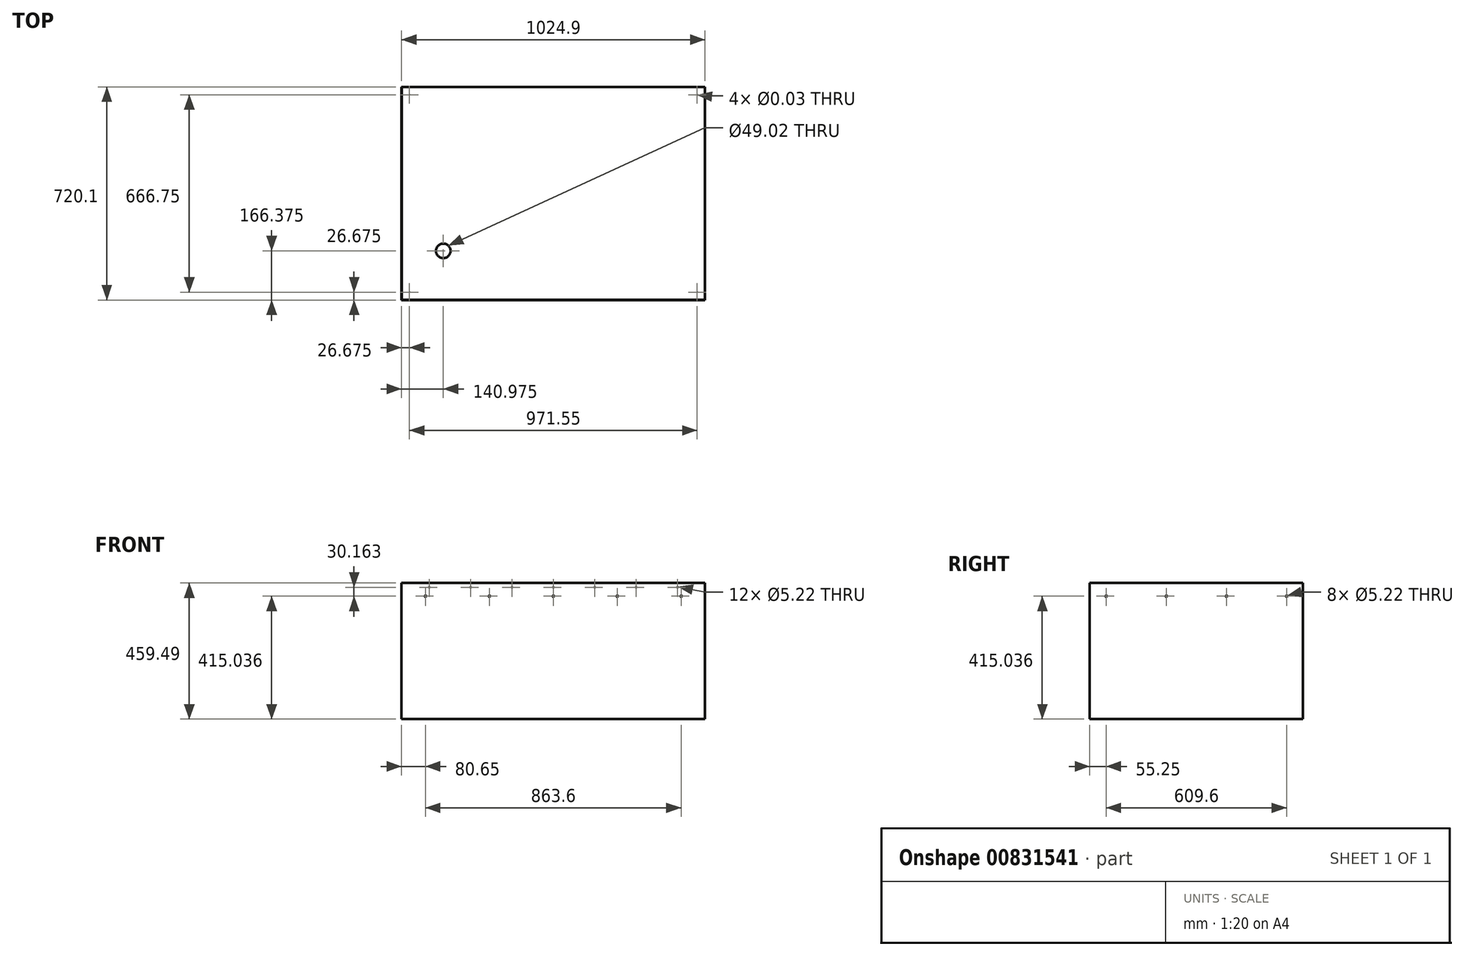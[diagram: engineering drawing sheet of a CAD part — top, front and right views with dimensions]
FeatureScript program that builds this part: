
annotation { "Feature Type Name" : "Feature", "Feature Type Description" : "" }
export const myFeature = defineFeature(function(context is Context, id is Id, definition is map)
    precondition{}
    {
        {
            var Q0;
            Q0=qCreatedBy(makeId("Top.planeOp"),FACE);
            var sketch = newSketch(context, id + "F0", { "sketchPlane" : qUnion([Q0])});
            skLineSegment(sketch, "E0.bottom", {"start": v(-512.45, 360.05) * mm, "end": v(512.45, 360.05) * mm});
            skLineSegment(sketch, "E0.top", {"start": v(-512.45, -360.05) * mm, "end": v(512.45, -360.05) * mm});
            skLineSegment(sketch, "E0.left", {"start": v(-512.44, 360.04) * mm, "end": v(-512.45, -360.05) * mm});
            skLineSegment(sketch, "E0.right", {"start": v(512.45, 360.05) * mm, "end": v(512.44, -360.05) * mm});
            skLineSegment(sketch, "E1", {"start": v(0, 360.05) * mm, "end": v(0, 0) * mm});
            skLineSegment(sketch, "E2", {"start": v(0, 0) * mm, "end": v(0, -360.05) * mm});
            skSolve(sketch);
        }
        {
            var Q0;
            Q0=makeQuery(id+"F0.imprint","IMPRINT",FACE,{"disambiguationData":[TD([[makeQuery(id+"F0.imprint","IMPRINT",EDGE,{"derivedFrom":sQuery(id+"F0.wireOp",EDGE,"E0.bottom")}),-1.0]])]});
            extrude(context, id + "F1", {"entities" : qUnion([Q0]), "depth" : 459.5 * mm, "offsetDistance" : 25.4 * mm});
        }
        {
            var Q0;
            Q0=makeQuery(id+"F1.opExtrude","CAP_FACE",FACE,{"disambiguationData":[OSD([sQuery(id+"F0.wireOp",EDGE,"E0.bottom"),sQuery(id+"F0.wireOp",EDGE,"E0.top"),sQuery(id+"F0.wireOp",EDGE,"E0.left"),sQuery(id+"F0.wireOp",EDGE,"E0.right"),sQuery(id+"F0.wireOp",EDGE,"5e8189b1-4f6e-42a7-91f4-dac5e5891543.filletArc"),sQuery(id+"F0.wireOp",EDGE,"1cc928d6-0298-44d3-bfd6-6e0c63f41985.filletArc"),sQuery(id+"F0.wireOp",EDGE,"5963119c-fd0b-4c36-9543-9db4226832d0.filletArc"),sQuery(id+"F0.wireOp",EDGE,"1aff30c5-95b7-47c3-b3d6-6abb8407ea33.filletArc")])],"isStart":false});
            shell(context, id + "F2", {"entities" : qUnion([Q0]), "thickness" : 0.76 * mm});
        }
        {
            var Q0;
            Q0=makeQuery(id+"F1.opExtrude","SWEPT_FACE",FACE,{"disambiguationData":[OSD([sQuery(id+"F0.wireOp",EDGE,"E0.top")])]});
            var sketch = newSketch(context, id + "F3", { "sketchPlane" : qUnion([Q0])});
            skPoint(sketch, "E3", {"position": v(-431.8, 415.04) * mm});
            skPoint(sketch, "E4", {"position": v(-215.9, 415.04) * mm});
            skPoint(sketch, "E5", {"position": v(0, 415.04) * mm});
            skPoint(sketch, "E6", {"position": v(215.9, 415.04) * mm});
            skPoint(sketch, "E7", {"position": v(431.8, 415.04) * mm});
            skLineSegment(sketch, "E8", {"start": v(-431.8, 415.04) * mm, "end": v(-215.9, 415.04) * mm});
            skLineSegment(sketch, "E9", {"start": v(0, 415.04) * mm, "end": v(-215.9, 415.04) * mm});
            skLineSegment(sketch, "E10", {"start": v(0, 415.04) * mm, "end": v(215.9, 415.04) * mm});
            skLineSegment(sketch, "E11", {"start": v(431.8, 415.04) * mm, "end": v(215.9, 415.04) * mm});
            skLineSegment(sketch, "E12", {"start": v(0, 459.49) * mm, "end": v(0, 415.04) * mm});
            skSolve(sketch);
        }
        {
            var Q0;
            Q0=makeQuery(id+"F1.opExtrude","SWEPT_FACE",FACE,{"disambiguationData":[OSD([sQuery(id+"F0.wireOp",EDGE,"E0.right")])]});
            var sketch = newSketch(context, id + "F4", { "sketchPlane" : qUnion([Q0])});
            skPoint(sketch, "E13", {"position": v(-304.8, 415.04) * mm});
            skPoint(sketch, "E14", {"position": v(-101.6, 415.04) * mm});
            skPoint(sketch, "E15", {"position": v(101.6, 415.04) * mm});
            skPoint(sketch, "E16", {"position": v(304.8, 415.04) * mm});
            skLineSegment(sketch, "E17", {"start": v(-304.8, 415.04) * mm, "end": v(-101.6, 415.04) * mm});
            skLineSegment(sketch, "E18", {"start": v(101.6, 415.04) * mm, "end": v(304.8, 415.04) * mm});
            skLineSegment(sketch, "E19", {"start": v(-101.6, 415.04) * mm, "end": v(101.6, 415.04) * mm});
            skLineSegment(sketch, "E20", {"start": v(0, 459.49) * mm, "end": v(0, 415.04) * mm});
            skSolve(sketch);
        }
        {
            var Q0;
            Q0=sQuery(id+"F3.wireOp",VERTEX,"E3");
            var Q1;
            Q1=sQuery(id+"F3.wireOp",VERTEX,"E4");
            var Q2;
            Q2=sQuery(id+"F3.wireOp",VERTEX,"E5");
            var Q3;
            Q3=sQuery(id+"F3.wireOp",VERTEX,"E6");
            var Q4;
            Q4=sQuery(id+"F3.wireOp",VERTEX,"E7");
            var Q5;
            Q5=makeQuery(id+"F1.opExtrude","SWEPT_BODY",BODY,{"disambiguationData":[OSD([sQuery(id+"F0.wireOp",EDGE,"E0.bottom"),sQuery(id+"F0.wireOp",EDGE,"E0.top"),sQuery(id+"F0.wireOp",EDGE,"E0.left"),sQuery(id+"F0.wireOp",EDGE,"E0.right"),sQuery(id+"F0.wireOp",EDGE,"5e8189b1-4f6e-42a7-91f4-dac5e5891543.filletArc"),sQuery(id+"F0.wireOp",EDGE,"1cc928d6-0298-44d3-bfd6-6e0c63f41985.filletArc"),sQuery(id+"F0.wireOp",EDGE,"5963119c-fd0b-4c36-9543-9db4226832d0.filletArc"),sQuery(id+"F0.wireOp",EDGE,"1aff30c5-95b7-47c3-b3d6-6abb8407ea33.filletArc")])]});
            hole(context, id + "F5", {"style" : HoleStyle.SIMPLE, "endStyle" : HoleEndStyle.BLIND, "standardTappedOrClearance" : lookupTablePath({ "standard" : "ANSI", "size" : "#5 (0.2)", "type" : "Drilled" }), "standardBlindInLast" : lookupTablePath({ "standard" : "ANSI", "size" : "#5 (0.2)", "type" : "Drilled" }), "holeDiameter" : 5.22 * mm, "majorDiameter" : 6.35 * mm, "holeDepth" : 0.76 * mm, "isTappedThrough" : true, "tappedDepth" : 12.7 * mm, "tapClearance" : 3, "locations" : qUnion([Q0, Q1, Q2, Q3, Q4]), "scope" : qUnion([Q5])});
        }
        {
            var Q0;
            Q0=sQuery(id+"F4.wireOp",VERTEX,"E13");
            var Q1;
            Q1=sQuery(id+"F4.wireOp",VERTEX,"E14");
            var Q2;
            Q2=sQuery(id+"F4.wireOp",VERTEX,"E15");
            var Q3;
            Q3=sQuery(id+"F4.wireOp",VERTEX,"E16");
            var Q4;
            Q4=makeQuery(id+"F1.opExtrude","SWEPT_BODY",BODY,{"disambiguationData":[OSD([sQuery(id+"F0.wireOp",EDGE,"E0.bottom"),sQuery(id+"F0.wireOp",EDGE,"E0.top"),sQuery(id+"F0.wireOp",EDGE,"E0.left"),sQuery(id+"F0.wireOp",EDGE,"E0.right"),sQuery(id+"F0.wireOp",EDGE,"5e8189b1-4f6e-42a7-91f4-dac5e5891543.filletArc"),sQuery(id+"F0.wireOp",EDGE,"1cc928d6-0298-44d3-bfd6-6e0c63f41985.filletArc"),sQuery(id+"F0.wireOp",EDGE,"5963119c-fd0b-4c36-9543-9db4226832d0.filletArc"),sQuery(id+"F0.wireOp",EDGE,"1aff30c5-95b7-47c3-b3d6-6abb8407ea33.filletArc")])]});
            hole(context, id + "F6", {"style" : HoleStyle.SIMPLE, "endStyle" : HoleEndStyle.THROUGH, "standardTappedOrClearance" : lookupTablePath({ "standard" : "ANSI", "size" : "#5 (0.2)", "type" : "Drilled" }), "standardBlindInLast" : lookupTablePath({ "standard" : "ANSI", "size" : "#5 (0.2)", "type" : "Drilled" }), "holeDiameter" : 5.22 * mm, "majorDiameter" : 6.35 * mm, "isTappedThrough" : true, "tappedDepth" : 12.7 * mm, "tapClearance" : 3, "locations" : qUnion([Q0, Q1, Q2, Q3]), "scope" : qUnion([Q4])});
        }
        {
            var Q0;
            Q0=makeQuery(id+"F2.opShell","OFFSET_FACE",FACE,{"disambiguationData":[OSD([sQuery(id+"F0.wireOp",EDGE,"E0.bottom"),sQuery(id+"F0.wireOp",EDGE,"E0.top"),sQuery(id+"F0.wireOp",EDGE,"E0.left"),sQuery(id+"F0.wireOp",EDGE,"E0.right")])]});
            var sketch = newSketch(context, id + "F7", { "sketchPlane" : qUnion([Q0])});
            skPoint(sketch, "E21", {"position": v(-371.48, -193.68) * mm});
            skSolve(sketch);
        }
        {
            var Q0;
            Q0=sQuery(id+"F7.wireOp",VERTEX,"E21");
            var Q1;
            Q1=makeQuery(id+"F1.opExtrude","SWEPT_BODY",BODY,{"disambiguationData":[OSD([sQuery(id+"F0.wireOp",EDGE,"E0.bottom"),sQuery(id+"F0.wireOp",EDGE,"E0.top"),sQuery(id+"F0.wireOp",EDGE,"E0.left"),sQuery(id+"F0.wireOp",EDGE,"E0.right")])]});
            hole(context, id + "F8", {"style" : HoleStyle.SIMPLE, "endStyle" : HoleEndStyle.THROUGH, "holeDiameter" : 49.02 * mm, "majorDiameter" : 6.35 * mm, "isTappedThrough" : true, "tappedDepth" : 12.7 * mm, "tapClearance" : 3, "locations" : qUnion([Q0]), "scope" : qUnion([Q1])});
        }
        {
            var Q0;
            Q0=makeQuery(id+"F2.opShell","OFFSET_FACE",FACE,{"disambiguationData":[OSD([sQuery(id+"F0.wireOp",EDGE,"E0.bottom"),sQuery(id+"F0.wireOp",EDGE,"E0.top"),sQuery(id+"F0.wireOp",EDGE,"E0.left"),sQuery(id+"F0.wireOp",EDGE,"E0.right")])]});
            var sketch = newSketch(context, id + "F9", { "sketchPlane" : qUnion([Q0])});
            skPoint(sketch, "E22", {"position": v(-485.78, 333.38) * mm});
            skPoint(sketch, "E23", {"position": v(485.78, 333.38) * mm});
            skPoint(sketch, "E24", {"position": v(485.78, -333.38) * mm});
            skPoint(sketch, "E25", {"position": v(-485.78, -333.38) * mm});
            skLineSegment(sketch, "E26.bottom", {"start": v(-485.78, 333.38) * mm, "end": v(485.78, 333.38) * mm});
            skLineSegment(sketch, "E26.top", {"start": v(-485.78, -333.38) * mm, "end": v(485.78, -333.38) * mm});
            skLineSegment(sketch, "E26.left", {"start": v(-485.78, 333.38) * mm, "end": v(-485.78, -333.38) * mm});
            skLineSegment(sketch, "E26.right", {"start": v(485.78, 333.38) * mm, "end": v(485.78, -333.38) * mm});
            skLineSegment(sketch, "E27.bottom", {"start": v(-517.52, 365.13) * mm, "end": v(517.52, 365.13) * mm});
            skLineSegment(sketch, "E27.top", {"start": v(-517.52, -365.13) * mm, "end": v(517.52, -365.13) * mm});
            skLineSegment(sketch, "E27.left", {"start": v(-517.52, 365.13) * mm, "end": v(-517.52, -365.13) * mm});
            skLineSegment(sketch, "E27.right", {"start": v(517.52, 365.13) * mm, "end": v(517.52, -365.13) * mm});
            skLineSegment(sketch, "E28", {"start": v(0, 365.13) * mm, "end": v(0, 359.28) * mm, "construction": true});
            skLineSegment(sketch, "E29", {"start": v(0, -365.13) * mm, "end": v(0, -359.28) * mm, "construction": true});
            skSolve(sketch);
        }
        {
            var Q0;
            Q0=sQuery(id+"F9.wireOp",VERTEX,"E22");
            var Q1;
            Q1=sQuery(id+"F9.wireOp",VERTEX,"E25");
            var Q2;
            Q2=sQuery(id+"F9.wireOp",VERTEX,"E24");
            var Q3;
            Q3=sQuery(id+"F9.wireOp",VERTEX,"E23");
            var Q4;
            Q4=makeQuery(id+"F1.opExtrude","SWEPT_BODY",BODY,{"disambiguationData":[OSD([sQuery(id+"F0.wireOp",EDGE,"E0.bottom"),sQuery(id+"F0.wireOp",EDGE,"E0.top"),sQuery(id+"F0.wireOp",EDGE,"E0.left"),sQuery(id+"F0.wireOp",EDGE,"E0.right")])]});
            hole(context, id + "F10", {"style" : HoleStyle.SIMPLE, "endStyle" : HoleEndStyle.THROUGH, "standardTappedOrClearance" : lookupTablePath({ "standard" : "ANSI", "size" : "11/16 (0.69)", "type" : "Drilled" }), "standardBlindInLast" : lookupTablePath({ "standard" : "ANSI", "size" : "11/16 (0.69)", "type" : "Drilled" }), "holeDiameter" : 11 / 406.4 * mm, "majorDiameter" : 6.35 * mm, "isTappedThrough" : true, "tappedDepth" : 12.7 * mm, "tapClearance" : 3, "locations" : qUnion([Q0, Q1, Q2, Q3]), "scope" : qUnion([Q4])});
        }
        {
            var Q0;
            Q0=makeQuery(id+"F2.opShell","OFFSET_FACE",FACE,{"disambiguationData":[OSD([sQuery(id+"F0.wireOp",EDGE,"E0.bottom"),sQuery(id+"F0.wireOp",EDGE,"E0.top"),sQuery(id+"F0.wireOp",EDGE,"E0.left"),sQuery(id+"F0.wireOp",EDGE,"E0.right")])]});
            var sketch = newSketch(context, id + "F11", { "sketchPlane" : qUnion([Q0])});
            skLineSegment(sketch, "E30", {"start": v(-513.56, 259.56) * mm, "end": v(-411.96, 361.16) * mm});
            skLineSegment(sketch, "E31", {"start": v(-411.96, 361.16) * mm, "end": v(-513.56, 361.16) * mm});
            skLineSegment(sketch, "E32", {"start": v(-513.56, 361.16) * mm, "end": v(-513.56, 259.56) * mm});
            skSolve(sketch);
        }
        {
            var Q0;
            Q0=makeQuery(id+"F1.opExtrude","SWEPT_FACE",FACE,{"disambiguationData":[OSD([sQuery(id+"F0.wireOp",EDGE,"E0.bottom")])]});
            var sketch = newSketch(context, id + "F12", { "sketchPlane" : qUnion([Q0])});
            skPoint(sketch, "E33", {"position": v(-419.1, 445.2) * mm});
            skPoint(sketch, "E34", {"position": v(-279.4, 445.2) * mm});
            skPoint(sketch, "E35", {"position": v(-139.7, 445.2) * mm});
            skPoint(sketch, "E36", {"position": v(0, 445.2) * mm});
            skPoint(sketch, "E37", {"position": v(139.7, 445.2) * mm});
            skPoint(sketch, "E38", {"position": v(279.4, 445.2) * mm});
            skPoint(sketch, "E39", {"position": v(419.1, 445.2) * mm});
            skLineSegment(sketch, "E40", {"start": v(-419.1, 445.2) * mm, "end": v(-279.4, 445.2) * mm, "construction": true});
            skLineSegment(sketch, "E41", {"start": v(-139.7, 445.2) * mm, "end": v(-279.4, 445.2) * mm, "construction": true});
            skLineSegment(sketch, "E42", {"start": v(-139.7, 445.2) * mm, "end": v(0, 445.2) * mm, "construction": true});
            skLineSegment(sketch, "E43", {"start": v(0, 445.2) * mm, "end": v(139.7, 445.2) * mm, "construction": true});
            skLineSegment(sketch, "E44", {"start": v(139.7, 445.2) * mm, "end": v(279.4, 445.2) * mm, "construction": true});
            skLineSegment(sketch, "E45", {"start": v(279.4, 445.2) * mm, "end": v(419.1, 445.2) * mm, "construction": true});
            skLineSegment(sketch, "E46", {"start": v(0, 445.2) * mm, "end": v(0, 459.49) * mm, "construction": true});
            skSolve(sketch);
        }
        {
            var Q0;
            Q0=sQuery(id+"F12.wireOp",VERTEX,"E33");
            var Q1;
            Q1=sQuery(id+"F12.wireOp",VERTEX,"E34");
            var Q2;
            Q2=sQuery(id+"F12.wireOp",VERTEX,"E35");
            var Q3;
            Q3=sQuery(id+"F12.wireOp",VERTEX,"E36");
            var Q4;
            Q4=sQuery(id+"F12.wireOp",VERTEX,"E37");
            var Q5;
            Q5=sQuery(id+"F12.wireOp",VERTEX,"E38");
            var Q6;
            Q6=sQuery(id+"F12.wireOp",VERTEX,"E39");
            var Q7;
            Q7=makeQuery(id+"F1.opExtrude","SWEPT_BODY",BODY,{"disambiguationData":[OSD([sQuery(id+"F0.wireOp",EDGE,"E0.bottom"),sQuery(id+"F0.wireOp",EDGE,"E0.top"),sQuery(id+"F0.wireOp",EDGE,"E0.left"),sQuery(id+"F0.wireOp",EDGE,"E0.right")])]});
            hole(context, id + "F13", {"style" : HoleStyle.SIMPLE, "endStyle" : HoleEndStyle.BLIND, "standardTappedOrClearance" : lookupTablePath({ "standard" : "ANSI", "size" : "#5 (0.2)", "type" : "Drilled" }), "standardBlindInLast" : lookupTablePath({ "standard" : "ANSI", "size" : "#5 (0.2)", "type" : "Drilled" }), "holeDiameter" : 5.22 * mm, "majorDiameter" : 6.35 * mm, "holeDepth" : 0.76 * mm, "isTappedThrough" : true, "tappedDepth" : 12.7 * mm, "tapClearance" : 3, "locations" : qUnion([Q0, Q1, Q2, Q3, Q4, Q5, Q6]), "scope" : qUnion([Q7])});
        }
    });
